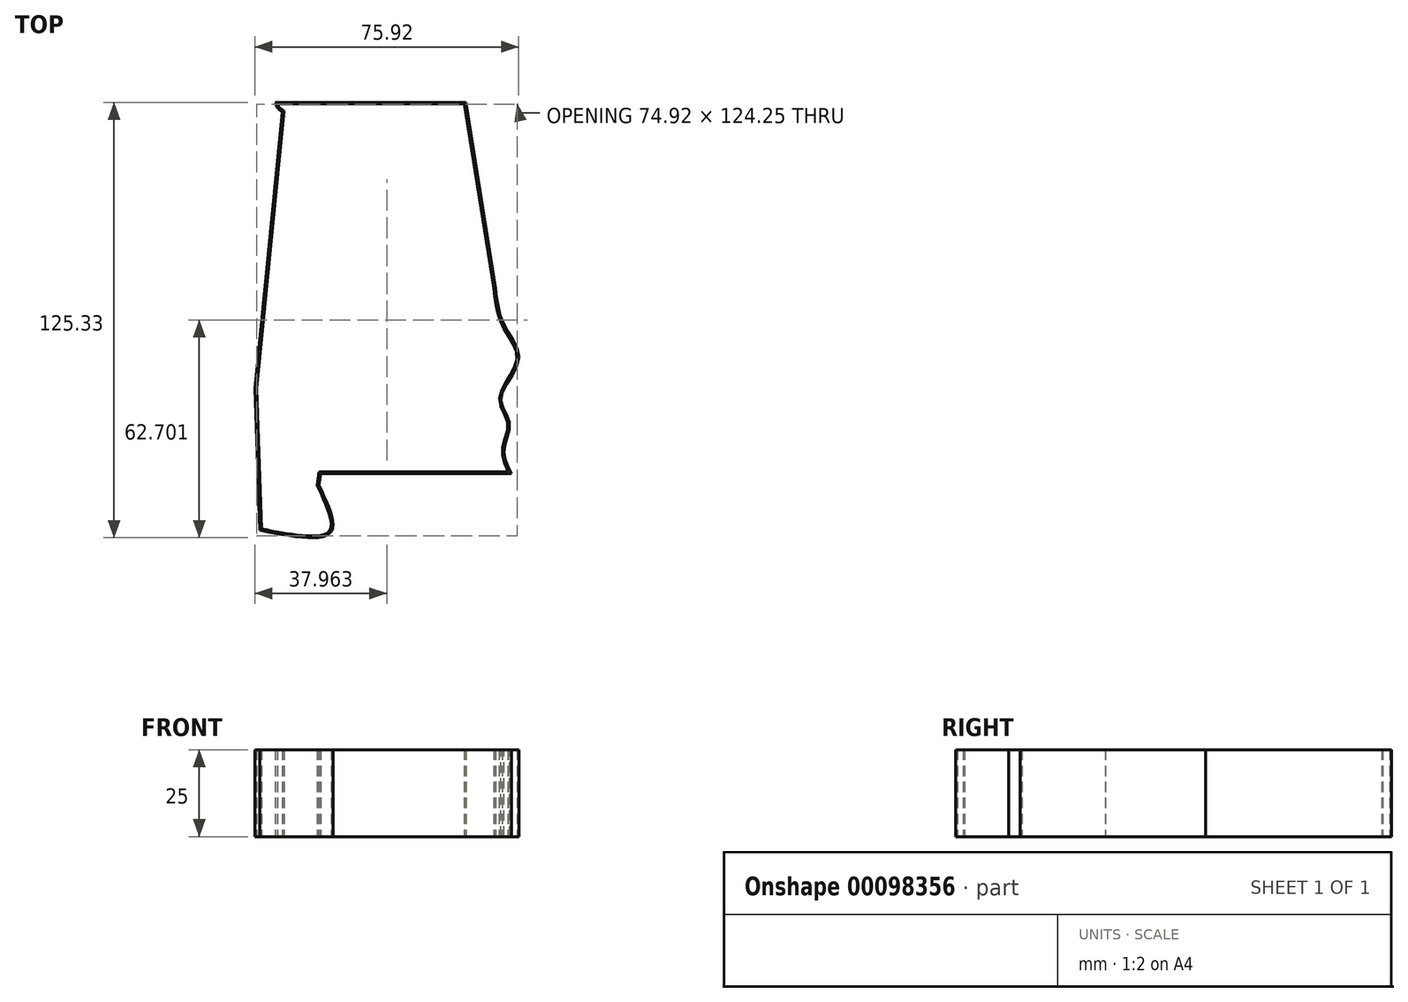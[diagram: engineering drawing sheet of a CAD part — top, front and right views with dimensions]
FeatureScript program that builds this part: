
annotation { "Feature Type Name" : "Feature", "Feature Type Description" : "" }
export const myFeature = defineFeature(function(context is Context, id is Id, definition is map)
    precondition{}
    {
        {
            var Q0;
            Q0=qCreatedBy(makeId("Top.planeOp"),FACE);
            var sketch = newSketch(context, id + "F0", { "sketchPlane" : qUnion([Q0])});
            skFitSpline(sketch, "E0", {"points": [v(-32.4, 59.22) * mm, v(-33.82, 60.42) * mm, v(-34.38, 61.98) * mm], "startDerivative": vector(-3.16, 2.11) * mm, "endDerivative": vector(-0.78, 3.41) * mm});
            skLineSegment(sketch, "E1", {"start": v(-34.38, 61.98) * mm, "end": v(20.41, 61.98) * mm});
            skLineSegment(sketch, "E2", {"start": v(20.41, 61.98) * mm, "end": v(28.98, 8.48) * mm});
            skLineSegment(sketch, "E3", {"start": v(33.52, -44.83) * mm, "end": v(-21.38, -44.83) * mm});
            skLineSegment(sketch, "E4", {"start": v(-21.38, -44.83) * mm, "end": v(-21.88, -48.14) * mm});
            skLineSegment(sketch, "E5", {"start": v(-38.9, -61.19) * mm, "end": v(-40.3, -20.34) * mm});
            skLineSegment(sketch, "E6", {"start": v(-40.3, -20.34) * mm, "end": v(-32.4, 59.22) * mm});
            skFitSpline(sketch, "E7", {"points": [v(-21.88, -48.14) * mm, v(-18.52, -61.8) * mm, v(-38.9, -61.19) * mm], "startDerivative": vector(17.56, -37.22) * mm, "endDerivative": vector(-49.53, 9.67) * mm});
            skFitSpline(sketch, "E8", {"points": [v(28.98, 8.48) * mm, v(31.4, -2.13) * mm, v(35.58, -12.06) * mm, v(30.54, -23.15) * mm, v(32.94, -30.29) * mm, v(31.4, -38.28) * mm, v(33.52, -44.83) * mm], "startDerivative": vector(6.12, -60.21) * mm, "endDerivative": vector(24, -43.78) * mm});
            skSolve(sketch);
        }
        {
            var Q0;
            Q0 = qSketchRegion(id + "F0", true);
            extrude(context, id + "F1", {"entities" : qUnion([Q0]), "depth" : 2 * mm, "offsetDistance" : 25 * mm});
        }
        {
            var Q0;
            Q0=makeQuery(id+"F1.opExtrude","SWEPT_BODY",BODY,{"disambiguationData":[OSD([sQuery(id+"F0.wireOp",EDGE,"E0"),sQuery(id+"F0.wireOp",EDGE,"E1"),sQuery(id+"F0.wireOp",EDGE,"E2"),sQuery(id+"F0.wireOp",EDGE,"2adae895-4ab8-4f2c-989a-873498c6d6ba"),sQuery(id+"F0.wireOp",EDGE,"E3"),sQuery(id+"F0.wireOp",EDGE,"E4"),sQuery(id+"F0.wireOp",EDGE,"456588a0-215a-484b-81c5-c4ee2efbdd4c"),sQuery(id+"F0.wireOp",EDGE,"E5"),sQuery(id+"F0.wireOp",EDGE,"E6"),sQuery(id+"F0.wireOp",EDGE,"810d8505-37a9-48c0-9c43-ea6a73d85bc3"),sQuery(id+"F0.wireOp",EDGE,"121438d1-1fe3-4721-9852-fcf507d36f00"),sQuery(id+"F0.wireOp",EDGE,"8c2a810e-cfd4-401c-839d-00235bfcba27"),sQuery(id+"F0.wireOp",EDGE,"d2877efc-34f6-4dc5-a6c0-a80a13e37e3b")])]});
            transform(context, id + "F2", {"entities" : qUnion([Q0]), "transformType" : TransformType.TRANSLATION_3D, "dx" : 0 * mm, "dy" : 0 * mm, "dz" : 0 * mm, "makeCopy" : true});
        }
        {
            var Q0;
            Q0=makeQuery(id+"F1.opExtrude","CAP_FACE",FACE,{"disambiguationData":[OSD([sQuery(id+"F0.wireOp",EDGE,"E0"),sQuery(id+"F0.wireOp",EDGE,"E1"),sQuery(id+"F0.wireOp",EDGE,"E2"),sQuery(id+"F0.wireOp",EDGE,"2adae895-4ab8-4f2c-989a-873498c6d6ba"),sQuery(id+"F0.wireOp",EDGE,"E3"),sQuery(id+"F0.wireOp",EDGE,"E4"),sQuery(id+"F0.wireOp",EDGE,"456588a0-215a-484b-81c5-c4ee2efbdd4c"),sQuery(id+"F0.wireOp",EDGE,"E5"),sQuery(id+"F0.wireOp",EDGE,"E6"),sQuery(id+"F0.wireOp",EDGE,"810d8505-37a9-48c0-9c43-ea6a73d85bc3"),sQuery(id+"F0.wireOp",EDGE,"121438d1-1fe3-4721-9852-fcf507d36f00"),sQuery(id+"F0.wireOp",EDGE,"8c2a810e-cfd4-401c-839d-00235bfcba27"),sQuery(id+"F0.wireOp",EDGE,"d2877efc-34f6-4dc5-a6c0-a80a13e37e3b")])],"isStart":false});
            extrude(context, id + "F3", {"entities" : qUnion([Q0]), "operationType" : NewBodyOperationType.ADD, "depth" : 23 * mm, "offsetDistance" : 25 * mm});
        }
        {
            var Q0;
            Q0=makeQuery(id+"F3.opExtrude","CAP_FACE",FACE,{"disambiguationData":[OSD([sQuery(id+"F0.wireOp",EDGE,"E0"),sQuery(id+"F0.wireOp",EDGE,"E1"),sQuery(id+"F0.wireOp",EDGE,"E2"),sQuery(id+"F0.wireOp",EDGE,"2adae895-4ab8-4f2c-989a-873498c6d6ba"),sQuery(id+"F0.wireOp",EDGE,"E3"),sQuery(id+"F0.wireOp",EDGE,"E4"),sQuery(id+"F0.wireOp",EDGE,"456588a0-215a-484b-81c5-c4ee2efbdd4c"),sQuery(id+"F0.wireOp",EDGE,"E5"),sQuery(id+"F0.wireOp",EDGE,"E6"),sQuery(id+"F0.wireOp",EDGE,"810d8505-37a9-48c0-9c43-ea6a73d85bc3"),sQuery(id+"F0.wireOp",EDGE,"121438d1-1fe3-4721-9852-fcf507d36f00"),sQuery(id+"F0.wireOp",EDGE,"8c2a810e-cfd4-401c-839d-00235bfcba27"),sQuery(id+"F0.wireOp",EDGE,"d2877efc-34f6-4dc5-a6c0-a80a13e37e3b")])],"isStart":false});
            var Q1;
            Q1=makeQuery(id+"F1.opExtrude","CAP_FACE",FACE,{"disambiguationData":[OSD([sQuery(id+"F0.wireOp",EDGE,"E0"),sQuery(id+"F0.wireOp",EDGE,"E1"),sQuery(id+"F0.wireOp",EDGE,"E2"),sQuery(id+"F0.wireOp",EDGE,"2adae895-4ab8-4f2c-989a-873498c6d6ba"),sQuery(id+"F0.wireOp",EDGE,"E3"),sQuery(id+"F0.wireOp",EDGE,"E4"),sQuery(id+"F0.wireOp",EDGE,"456588a0-215a-484b-81c5-c4ee2efbdd4c"),sQuery(id+"F0.wireOp",EDGE,"E5"),sQuery(id+"F0.wireOp",EDGE,"E6"),sQuery(id+"F0.wireOp",EDGE,"810d8505-37a9-48c0-9c43-ea6a73d85bc3"),sQuery(id+"F0.wireOp",EDGE,"121438d1-1fe3-4721-9852-fcf507d36f00"),sQuery(id+"F0.wireOp",EDGE,"8c2a810e-cfd4-401c-839d-00235bfcba27"),sQuery(id+"F0.wireOp",EDGE,"d2877efc-34f6-4dc5-a6c0-a80a13e37e3b")])],"isStart":true});
            shell(context, id + "F4", {"entities" : qUnion([Q0, Q1]), "thickness" : 0.5 * mm});
        }
    });
